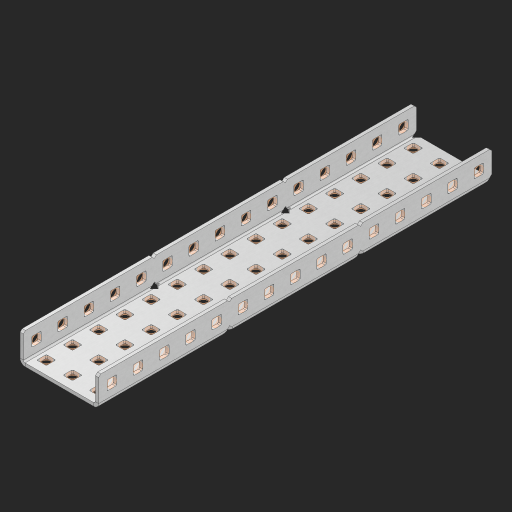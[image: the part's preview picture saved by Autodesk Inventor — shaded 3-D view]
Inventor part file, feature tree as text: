
AUTODESK INVENTOR PART (.ipt)
format: ipt  version: 2023 (Build 270158000, 158)  size: 1,142,272 bytes
history: native  units: in
note: dims shown in document units (in); Inventor stores cm internally (conversion verified against a paired STEP export)
features: other x80, extrude x74, sheet_metal_op x10, sketch x8, mirror x1, pattern_linear x1, chamfer x1
ambient origin geometry x8: Origin, YZ Plane, XZ Plane, XY Plane, X Axis, Y Axis, Z Axis, Center Point
bodies: Solid1 (feature_tree), Body (feature_tree)
feature tree (175):
  other  "Flange Pattern Plane"
  sheet_metal_op  "Flange Pattern"
  sheet_metal_op  "Body Pattern"
  other  "Arc Length"
  mirror  "Notch Mirror"
  pattern_linear  "Notch Pattern"  Spacing1=0.25in  [1 undecoded]
  chamfer  "End Chamfer"
  extrude  "Half Cut"  Depth=0.0625in
  sketch  "Sketch1"  dims[d0=1.5in]
  other  "Plate1"
  sketch  "Sketch2"  dims[d1=7.5in]
  other  "Plate2"
  sheet_metal_op  "Bend1"
  sheet_metal_op  "Corner1"
  sketch  "Sketch3"  dims[d2=0.0625in]
  other  "Flange Pattern Sketch"
  sketch  "Sketch7"  dims[d3=0.0625in]
  other  "Srf1"
  other  "Srf2"
  sketch  "Sketch8"  dims[d4=0.0312in]
  sketch  "Sketch9"  dims[d5=0.125in]
  other  "Srf91"
  sheet_metal_op  "Body Pattern Sketch"
  other  "Srf92"
  sketch  "Sketch13"  dims[d6=0.0625in]
  sketch  "Sketch14"  dims[d7=0.5in d8=90.0deg d9=0.0312in d10=0.25in d11=0.0625in d12=0.0625in d16=0.182in d17=0.02in d18=0.0625in d19=0.0in d20=0.25in d21=0.25in d46=0.172in d47=1.0in d48=0.0in d49=0.182in d50=0.02in d51=0.25in d52=0.25in d53=0.0625in d54=0.0in d55=0.172in d56=1.0in d57=0.0in d60=5.9055in d62=0.5in d63=1.1811in d65=0.5in d85=0.1473in d86=0.1782in d88=0.04in d89=0.0625in d90=0.0in d91=0.04in d92=0.0491in d95=2.5in d96=0.04in d97=0.25in d98=45.0deg d101=0.0in d102=2.497in d131=1.5in d132=5.9055in d134=0.5in d139=0.5in]
  other  "Srf856"
  other  "Srf1310"
  other  "Srf1311"
  other  "Srf1312"
  other  "Srf1376"
  other  "Srf1377"
  other  "Srf1728"
  other  "Srf1755"
  other  "Srf1878"
  other  "Srf1879"
  other  "Srf1880"
  other  "Srf1881"
  other  "Srf1882"
  other  "Srf1883"
  other  "Srf1884"
  other  "Srf1885"
  other  "Srf1886"
  other  "Srf1887"
  other  "Srf1888"
  other  "Srf1889"
  other  "Srf1890"
  other  "Srf1891"
  other  "Srf1892"
  other  "Srf1893"
  other  "Srf1894"
  other  "Srf1895"
  other  "Srf1896"
  other  "Srf1897"
  other  "Srf1898"
  other  "Srf1899"
  other  "Srf1900"
  other  "Srf1901"
  other  "Srf1942"
  other  "Srf1943"
  other  "Srf1944"
  other  "Srf1945"
  other  "Srf1946"
  other  "Srf1947"
  other  "Srf1948"
  other  "Srf1949"
  other  "Srf1950"
  other  "Srf1951"
  other  "Srf1952"
  other  "Srf1953"
  other  "Srf1954"
  other  "Srf1955"
  other  "Srf1956"
  other  "Srf1957"
  other  "Srf1958"
  other  "Srf1959"
  other  "Srf1960"
  other  "Srf1961"
  other  "Srf1962"
  other  "Srf1963"
  other  "Srf1964"
  other  "Srf1965"
  other  "Srf1966"
  other  "Srf1967"
  other  "Srf1968"
  other  "Srf1969"
  other  "Srf1970"
  other  "Srf1971"
  other  "Srf1972"
  other  "Srf1973"
  other  "Srf1974"
  other  "Srf1975"
  other  "Srf1976"
  other  "Srf1977"
  other  "Srf1978"
  other  "Srf1979"
  other  "Srf1980"
  sheet_metal_op  "Flange Stamp"
  sheet_metal_op  "Flange Circle"
  sheet_metal_op  "Body Stamp"
  sheet_metal_op  "Body Circle"
  sheet_metal_op  "Notch"
  extrude  "ExtrusionSrf2"  Depth=0.0625in
  extrude  "ExtrusionSrf92"  Depth=1.5in
  extrude  "ExtrusionSrf856"  Depth=0.02in
  extrude  "ExtrusionSrf1310"  Depth=0.0625in
  extrude  "ExtrusionSrf1311"  TaperAngle=0.0deg  [1 undecoded]
  extrude  "ExtrusionSrf1312"  Depth=0.25in
  extrude  "ExtrusionSrf1376"  Depth=0.25in
  extrude  "ExtrusionSrf1377"  Depth=1.5in
  extrude  "ExtrusionSrf1728"  Depth=1.5in TaperAngle=0.0deg
  extrude  "ExtrusionSrf1755"  Depth=1.5in
  extrude  "ExtrusionSrf1878"  Depth=0.02in
  extrude  "ExtrusionSrf1879"  Depth=0.25in
  extrude  "ExtrusionSrf1880"  Depth=0.25in
  extrude  "ExtrusionSrf1881"  Depth=0.0625in
  extrude  "ExtrusionSrf1882"  TaperAngle=0.0deg  [1 undecoded]
  extrude  "ExtrusionSrf1883"  Depth=1.5in
  extrude  "ExtrusionSrf1884"  Depth=1.5in TaperAngle=0.0deg
  extrude  "ExtrusionSrf1885"  Depth=1.5in
  extrude  "ExtrusionSrf1886"  Depth=1.5in
  extrude  "ExtrusionSrf1887"  Depth=1.5in
  extrude  "ExtrusionSrf1888"  Depth=1.5in
  extrude  "ExtrusionSrf1889"  Depth=1.5in
  extrude  "ExtrusionSrf1890"  Depth=0.0625in
  extrude  "ExtrusionSrf1891"  TaperAngle=0.0deg  [1 undecoded]
  extrude  "ExtrusionSrf1892"  Depth=1.5in
  extrude  "ExtrusionSrf1893"  Depth=1.5in
  extrude  "ExtrusionSrf1894"  Depth=1.5in
  extrude  "ExtrusionSrf1895"  Depth=0.25in TaperAngle=45.0deg
  extrude  "ExtrusionSrf1896"  TaperAngle=0.0deg  [1 undecoded]
  extrude  "ExtrusionSrf1897"  Depth=1.5in
  extrude  "ExtrusionSrf1898"  Depth=1.5in
  extrude  "ExtrusionSrf1899"  Depth=1.5in
  extrude  "ExtrusionSrf1900"  Depth=1.5in
  extrude  "ExtrusionSrf1901"  Depth=1.5in
  extrude  "ExtrusionSrf1942"  [1 undecoded]
  extrude  "ExtrusionSrf1943"  [1 undecoded]
  extrude  "ExtrusionSrf1944"  [1 undecoded]
  extrude  "ExtrusionSrf1945"  [1 undecoded]
  extrude  "ExtrusionSrf1946"  [1 undecoded]
  extrude  "ExtrusionSrf1947"  [1 undecoded]
  extrude  "ExtrusionSrf1948"  [1 undecoded]
  extrude  "ExtrusionSrf1949"  [1 undecoded]
  extrude  "ExtrusionSrf1950"  [1 undecoded]
  extrude  "ExtrusionSrf1951"  [1 undecoded]
  extrude  "ExtrusionSrf1952"  [1 undecoded]
  extrude  "ExtrusionSrf1953"  [1 undecoded]
  extrude  "ExtrusionSrf1954"  [1 undecoded]
  extrude  "ExtrusionSrf1955"  [1 undecoded]
  extrude  "ExtrusionSrf1956"  [1 undecoded]
  extrude  "ExtrusionSrf1957"  [1 undecoded]
  extrude  "ExtrusionSrf1958"  [1 undecoded]
  extrude  "ExtrusionSrf1959"  [1 undecoded]
  extrude  "ExtrusionSrf1960"  [1 undecoded]
  extrude  "ExtrusionSrf1961"  [1 undecoded]
  extrude  "ExtrusionSrf1962"  [1 undecoded]
  extrude  "ExtrusionSrf1963"  [1 undecoded]
  extrude  "ExtrusionSrf1964"  [1 undecoded]
  extrude  "ExtrusionSrf1965"  [1 undecoded]
  extrude  "ExtrusionSrf1966"  [1 undecoded]
  extrude  "ExtrusionSrf1967"  [1 undecoded]
  extrude  "ExtrusionSrf1968"  [1 undecoded]
  extrude  "ExtrusionSrf1969"  [1 undecoded]
  extrude  "ExtrusionSrf1970"  [1 undecoded]
  extrude  "ExtrusionSrf1971"  [1 undecoded]
  extrude  "ExtrusionSrf1972"  [1 undecoded]
  extrude  "ExtrusionSrf1973"  [1 undecoded]
  extrude  "ExtrusionSrf1974"  [1 undecoded]
  extrude  "ExtrusionSrf1975"  [1 undecoded]
  extrude  "ExtrusionSrf1976"  [1 undecoded]
  extrude  "ExtrusionSrf1977"  [1 undecoded]
  extrude  "ExtrusionSrf1978"  [1 undecoded]
  extrude  "ExtrusionSrf1979"  [1 undecoded]
  extrude  "ExtrusionSrf1980"  [1 undecoded]
note: 44 required parameter values undecoded (feature->parameter linkage not recoverable at this tier; creation-order binding heuristic only, values carry confidence <= 0.55)
